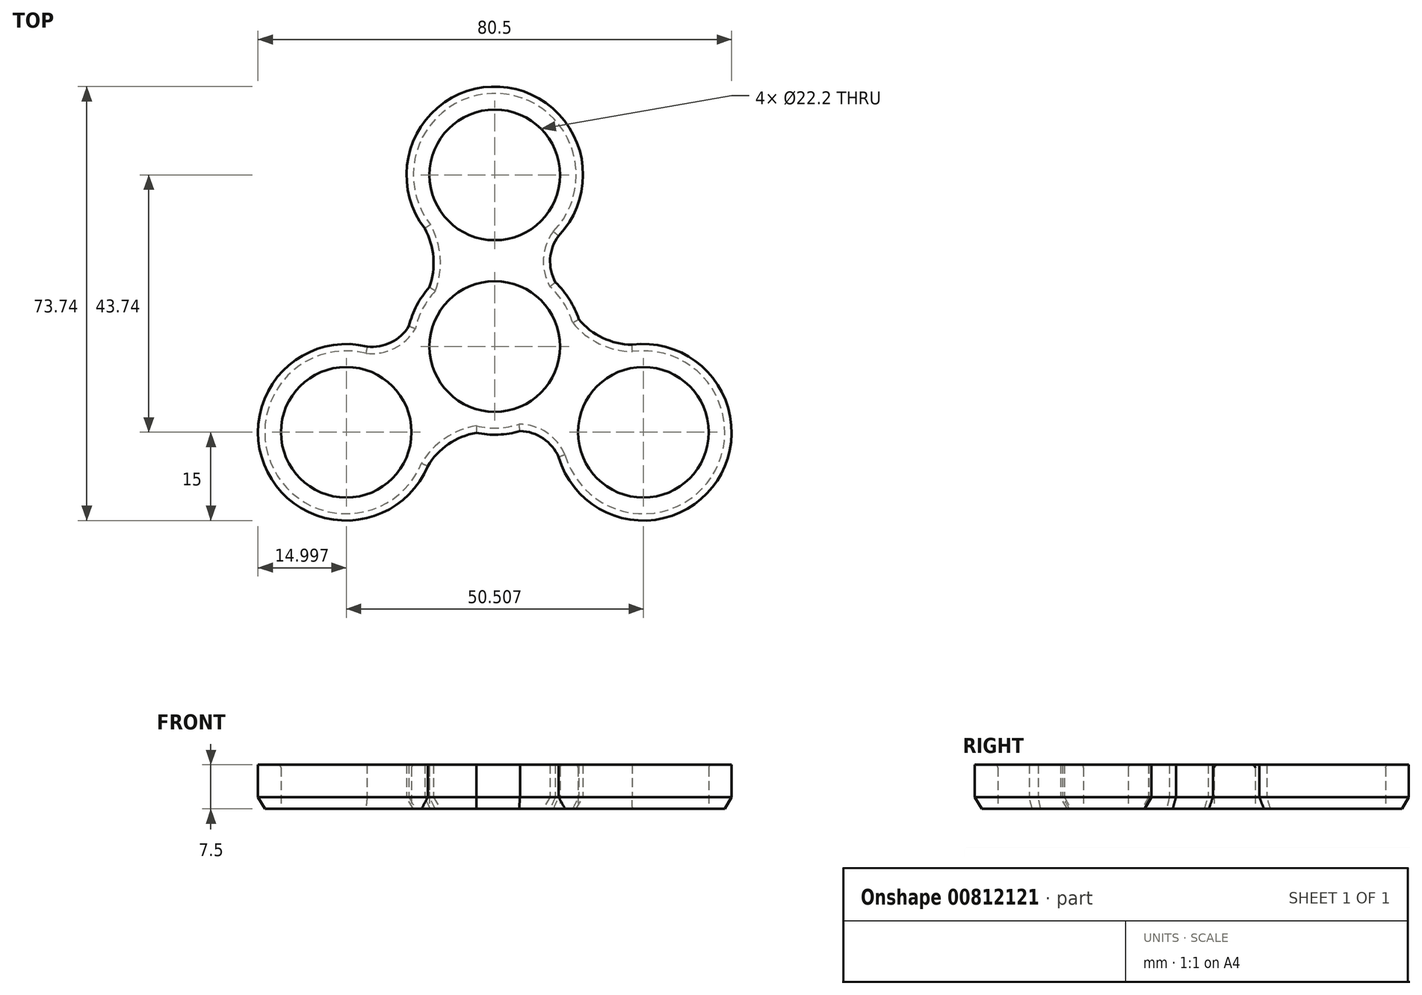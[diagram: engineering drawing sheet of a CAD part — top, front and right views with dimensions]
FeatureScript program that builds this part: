
annotation { "Feature Type Name" : "Feature", "Feature Type Description" : "" }
export const myFeature = defineFeature(function(context is Context, id is Id, definition is map)
    precondition{}
    {
        {
            var Q0;
            Q0=qCreatedBy(makeId("Top.planeOp"),FACE);
            var sketch = newSketch(context, id + "F0", { "sketchPlane" : qUnion([Q0])});
            skCircle(sketch, "E0", {"center": v(0, 0) * mm, "radius": 11.1 * mm});
            skCircle(sketch, "E1", {"center": v(0, 0) * mm, "radius": 15 * mm});
            skCircle(sketch, "E2", {"center": v(0, 29.16) * mm, "radius": 11.1 * mm});
            skCircle(sketch, "E3", {"center": v(0, 29.16) * mm, "radius": 15 * mm});
            skArc(sketch, "E4", {"start": v(-11.13, 10.06) * mm, "mid": v(-10.43, 15.14) * mm, "end": v(-11.92, 20.05) * mm});
            skArc(sketch, "E5", {"start": v(10.85, 18.8) * mm, "mid": v(9.41, 14.93) * mm, "end": v(10.3, 10.9) * mm});
            skCircle(sketch, "E6.1.0", {"center": v(-25.25, -14.58) * mm, "radius": 15 * mm});
            skCircle(sketch, "E6.1.1", {"center": v(-25.25, -14.58) * mm, "radius": 11.1 * mm});
            skArc(sketch, "E6.1.2", {"start": v(-3.15, -14.67) * mm, "mid": v(-7.9, -16.6) * mm, "end": v(-11.4, -20.35) * mm});
            skArc(sketch, "E6.1.3", {"start": v(-21.7, 0) * mm, "mid": v(-17.64, 0.69) * mm, "end": v(-14.6, 3.47) * mm});
            skCircle(sketch, "E6.2.0", {"center": v(25.25, -14.58) * mm, "radius": 15 * mm});
            skCircle(sketch, "E6.2.1", {"center": v(25.25, -14.58) * mm, "radius": 11.1 * mm});
            skArc(sketch, "E6.2.2", {"start": v(14.27, 4.6) * mm, "mid": v(18.33, 1.47) * mm, "end": v(23.33, 0.3) * mm});
            skArc(sketch, "E6.2.3", {"start": v(10.86, -18.8) * mm, "mid": v(8.22, -15.62) * mm, "end": v(4.29, -14.37) * mm});
            skSolve(sketch);
        }
        {
            var Q0;
            Q0=qSketchRegion(id+"F0",true);
            extrude(context, id + "F1", {"entities" : qUnion([Q0]), "depth" : 7.5 * mm, "offsetDistance" : 25 * mm});
        }
        {
            var Q0;
            {var subQ0=sQuery(id+"F0.wireOp",EDGE,"E6.2.0");var subQ1=sQuery(id+"F0.wireOp",EDGE,"E1");var subQ2=makeQuery(id+"F0.imprint","INTERSECT",VERTEX,{"disambiguationData":[OD(0.0)],"derivedFrom":[subQ1,subQ0]});Q0=makeQuery(id+"F0.imprint","IMPRINT",FACE,{"disambiguationData":[TD([[makeQuery(id+"F0.imprint","IMPRINT",EDGE,{"disambiguationData":[TD([[subQ2,-1.0]])],"derivedFrom":subQ1}),1.0]])]});}
            var Q1;
            {var subQ0=sQuery(id+"F0.wireOp",EDGE,"E6.1.0");var subQ1=sQuery(id+"F0.wireOp",EDGE,"E1");var subQ2=makeQuery(id+"F0.imprint","INTERSECT",VERTEX,{"disambiguationData":[OD(0.0)],"derivedFrom":[subQ1,subQ0]});Q1=makeQuery(id+"F0.imprint","IMPRINT",FACE,{"disambiguationData":[TD([[makeQuery(id+"F0.imprint","IMPRINT",EDGE,{"disambiguationData":[TD([[subQ2,-1.0]])],"derivedFrom":subQ1}),1.0]])]});}
            var Q2;
            {var subQ0=sQuery(id+"F0.wireOp",EDGE,"E3");var subQ1=sQuery(id+"F0.wireOp",EDGE,"E1");var subQ2=makeQuery(id+"F0.imprint","INTERSECT",VERTEX,{"disambiguationData":[OD(0.0)],"derivedFrom":[subQ1,subQ0]});Q2=makeQuery(id+"F0.imprint","IMPRINT",FACE,{"disambiguationData":[TD([[makeQuery(id+"F0.imprint","IMPRINT",EDGE,{"disambiguationData":[TD([[subQ2,-1.0]])],"derivedFrom":subQ1}),1.0]])]});}
            extrude(context, id + "F2", {"entities" : qUnion([Q0, Q1, Q2]), "operationType" : NewBodyOperationType.ADD, "depth" : 7.5 * mm, "offsetDistance" : 25 * mm});
        }
        {
            var Q0;
            Q0=makeQuery(id+"F1.opExtrude","CAP_EDGE",EDGE,{"disambiguationData":[OSD([sQuery(id+"F0.wireOp",EDGE,"E2")])],"isStart":false});
            var Q1;
            Q1=makeQuery(id+"F1.opExtrude","CAP_EDGE",EDGE,{"disambiguationData":[OSD([sQuery(id+"F0.wireOp",EDGE,"E0")])],"isStart":false});
            var Q2;
            Q2=makeQuery(id+"F1.opExtrude","CAP_EDGE",EDGE,{"disambiguationData":[OSD([sQuery(id+"F0.wireOp",EDGE,"E6.2.1")])],"isStart":false});
            var Q3;
            Q3=makeQuery(id+"F1.opExtrude","CAP_EDGE",EDGE,{"disambiguationData":[OSD([sQuery(id+"F0.wireOp",EDGE,"E6.1.1")])],"isStart":false});
            fillet(context, id + "F3", {"entities" : qUnion([Q0, Q1, Q2, Q3]), "radius" : 0.5 * mm, "tangentPropagation" : true, "allowEdgeOverflow" : false});
        }
        {
            var Q0;
            {var subQ0=sQuery(id+"F0.wireOp",EDGE,"E6.1.0");Q0=makeQuery(id+"F1.opExtrude","CAP_EDGE",EDGE,{"disambiguationData":[OSD([subQ0]),TDD([makeQuery(id+"F0.imprint","IMPRINT",EDGE,{"disambiguationData":[TD([[makeQuery(id+"F0.imprint","INTERSECT",VERTEX,{"derivedFrom":[subQ0,sQuery(id+"F0.wireOp",EDGE,"E6.1.2")]}),1.0]])],"derivedFrom":subQ0})])],"isStart":true});}
            var Q1;
            Q1=makeQuery(id+"F1.opExtrude","CAP_EDGE",EDGE,{"disambiguationData":[OSD([sQuery(id+"F0.wireOp",EDGE,"E6.1.3")])],"isStart":true});
            var Q2;
            Q2=makeQuery(id+"F1.opExtrude","CAP_EDGE",EDGE,{"disambiguationData":[OSD([sQuery(id+"F0.wireOp",EDGE,"E6.1.2")])],"isStart":true});
            var Q3;
            Q3=makeQuery(id+"F1.opExtrude","CAP_EDGE",EDGE,{"disambiguationData":[OSD([sQuery(id+"F0.wireOp",EDGE,"E6.2.3")])],"isStart":true});
            var Q4;
            {var subQ0=sQuery(id+"F0.wireOp",EDGE,"E6.2.0");Q4=makeQuery(id+"F1.opExtrude","CAP_EDGE",EDGE,{"disambiguationData":[OSD([subQ0]),TDD([makeQuery(id+"F0.imprint","IMPRINT",EDGE,{"disambiguationData":[TD([[makeQuery(id+"F0.imprint","INTERSECT",VERTEX,{"derivedFrom":[subQ0,sQuery(id+"F0.wireOp",EDGE,"E6.2.2")]}),1.0]])],"derivedFrom":subQ0})])],"isStart":true});}
            var Q5;
            Q5=makeQuery(id+"F1.opExtrude","CAP_EDGE",EDGE,{"disambiguationData":[OSD([sQuery(id+"F0.wireOp",EDGE,"E6.2.2")])],"isStart":true});
            var Q6;
            Q6=makeQuery(id+"F1.opExtrude","CAP_EDGE",EDGE,{"disambiguationData":[OSD([sQuery(id+"F0.wireOp",EDGE,"E5")])],"isStart":true});
            var Q7;
            {var subQ0=sQuery(id+"F0.wireOp",EDGE,"E3");Q7=makeQuery(id+"F1.opExtrude","CAP_EDGE",EDGE,{"disambiguationData":[OSD([subQ0]),TDD([makeQuery(id+"F0.imprint","IMPRINT",EDGE,{"disambiguationData":[TD([[makeQuery(id+"F0.imprint","INTERSECT",VERTEX,{"derivedFrom":[subQ0,sQuery(id+"F0.wireOp",EDGE,"E4")]}),1.0]])],"derivedFrom":subQ0})])],"isStart":true});}
            var Q8;
            Q8=makeQuery(id+"F1.opExtrude","CAP_EDGE",EDGE,{"disambiguationData":[OSD([sQuery(id+"F0.wireOp",EDGE,"E4")])],"isStart":true});
            var Q9;
            {var subQ0=sQuery(id+"F0.wireOp",EDGE,"E1");Q9=makeQuery(id+"F1.opExtrude","CAP_EDGE",EDGE,{"disambiguationData":[OSD([subQ0]),TDD([makeQuery(id+"F0.imprint","IMPRINT",EDGE,{"disambiguationData":[TD([[makeQuery(id+"F0.imprint","INTERSECT",VERTEX,{"derivedFrom":[subQ0,sQuery(id+"F0.wireOp",EDGE,"E5")]}),1.0]])],"derivedFrom":subQ0})])],"isStart":true});}
            var Q10;
            {var subQ0=sQuery(id+"F0.wireOp",EDGE,"E1");Q10=makeQuery(id+"F1.opExtrude","CAP_EDGE",EDGE,{"disambiguationData":[OSD([subQ0]),TDD([makeQuery(id+"F0.imprint","IMPRINT",EDGE,{"disambiguationData":[TD([[makeQuery(id+"F0.imprint","INTERSECT",VERTEX,{"derivedFrom":[subQ0,sQuery(id+"F0.wireOp",EDGE,"E4")]}),-1.0]])],"derivedFrom":subQ0})])],"isStart":true});}
            var Q11;
            {var subQ0=sQuery(id+"F0.wireOp",EDGE,"E1");Q11=makeQuery(id+"F1.opExtrude","CAP_EDGE",EDGE,{"disambiguationData":[OSD([subQ0]),TDD([makeQuery(id+"F0.imprint","IMPRINT",EDGE,{"disambiguationData":[TD([[makeQuery(id+"F0.imprint","INTERSECT",VERTEX,{"derivedFrom":[subQ0,sQuery(id+"F0.wireOp",EDGE,"E6.1.2")]}),-1.0]])],"derivedFrom":subQ0})])],"isStart":true});}
            chamfer(context, id + "F4", {"entities" : qUnion([Q0, Q1, Q2, Q3, Q4, Q5, Q6, Q7, Q8, Q9, Q10, Q11]), "chamferType" : ChamferType.OFFSET_ANGLE, "width" : 2 * mm, "oppositeDirection" : false, "angle" : 30 * degree, "tangentPropagation" : true});
        }
    });
